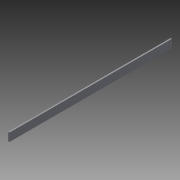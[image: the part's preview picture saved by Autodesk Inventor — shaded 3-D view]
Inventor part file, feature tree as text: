
AUTODESK INVENTOR PART (.ipt)
format: ipt  version: 2015 SP1 (Build 190203100, 203)  size: 69,120 bytes
history: native  units: in
note: dims shown in document units (in); Inventor stores cm internally (conversion verified against a paired STEP export)
features: extrude x1, sketch x1
ambient origin geometry x8: Origin, YZ Plane, XZ Plane, XY Plane, X Axis, Y Axis, Z Axis, Center Point
bodies: Solid1 (feature_tree)
feature tree (2):
  extrude  "Extrusion1"  Depth=0.6299in
  sketch  "Sketch1"  dims[d0=3.937in d1=0.6299in d2=78.7402in d3=0.0in]
